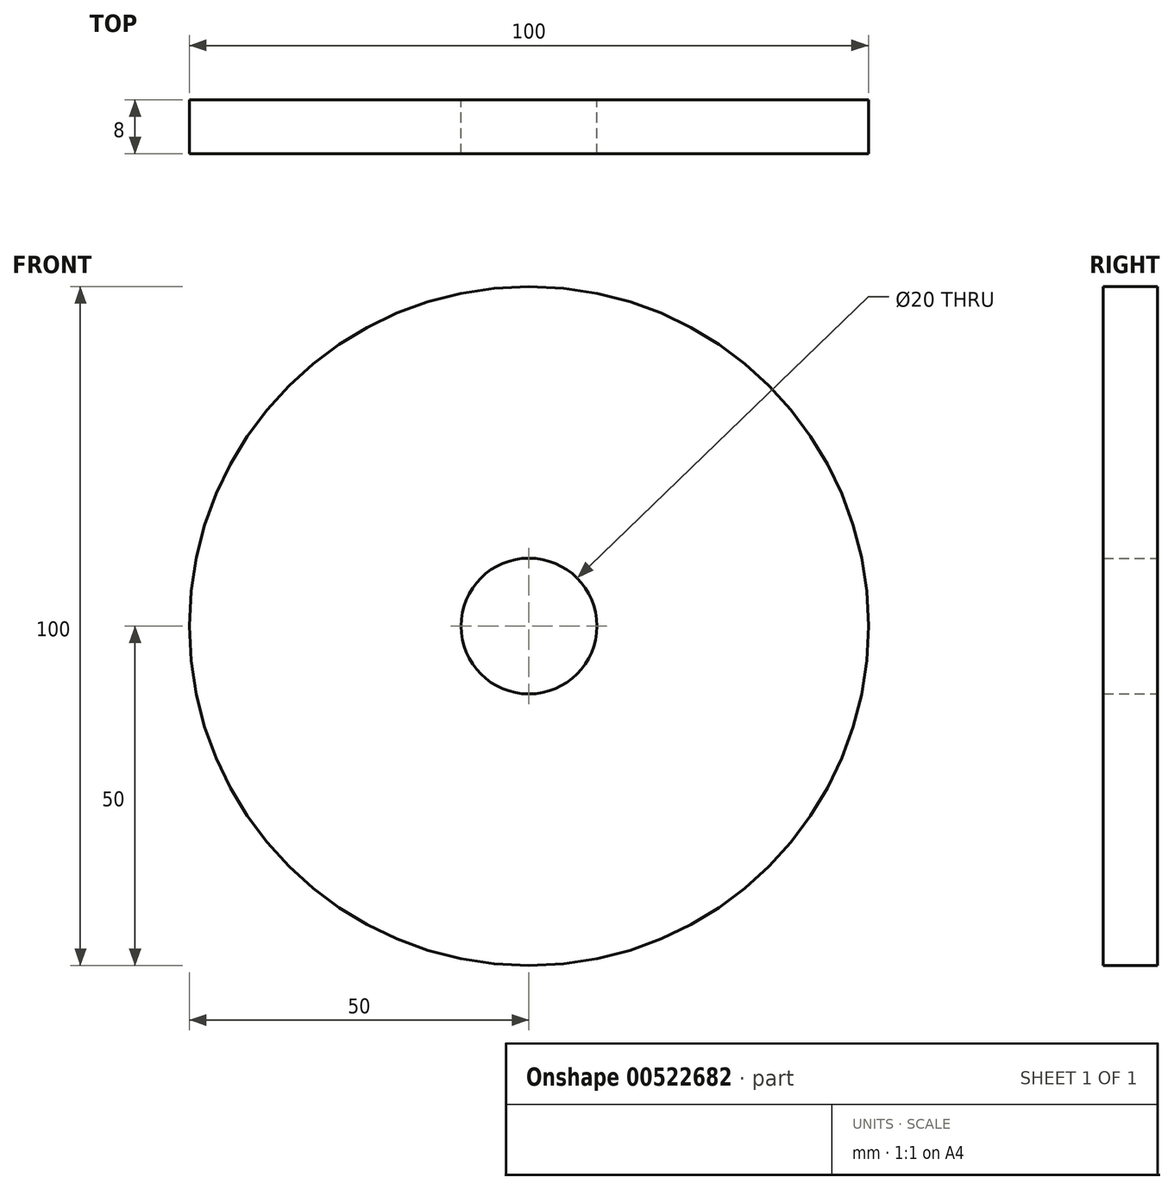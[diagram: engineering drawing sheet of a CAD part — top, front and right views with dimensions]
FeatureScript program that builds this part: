
annotation { "Feature Type Name" : "Feature", "Feature Type Description" : "" }
export const myFeature = defineFeature(function(context is Context, id is Id, definition is map)
    precondition{}
    {
        {
            var Q0;
            Q0=qCreatedBy(makeId("Front.planeOp"),FACE);
            var sketch = newSketch(context, id + "F0", { "sketchPlane" : qUnion([Q0])});
            skCircle(sketch, "E0", {"center": v(0, 0) * mm, "radius": 50 * mm});
            skCircle(sketch, "E1", {"center": v(0, 0) * mm, "radius": 10 * mm});
            skSolve(sketch);
        }
        {
            var Q0;
            Q0 = qSketchRegion(id + "F0", true);
            extrude(context, id + "F1", {"entities" : qUnion([Q0]), "depth" : 8 * mm, "offsetDistance" : 25 * mm});
        }
    });
